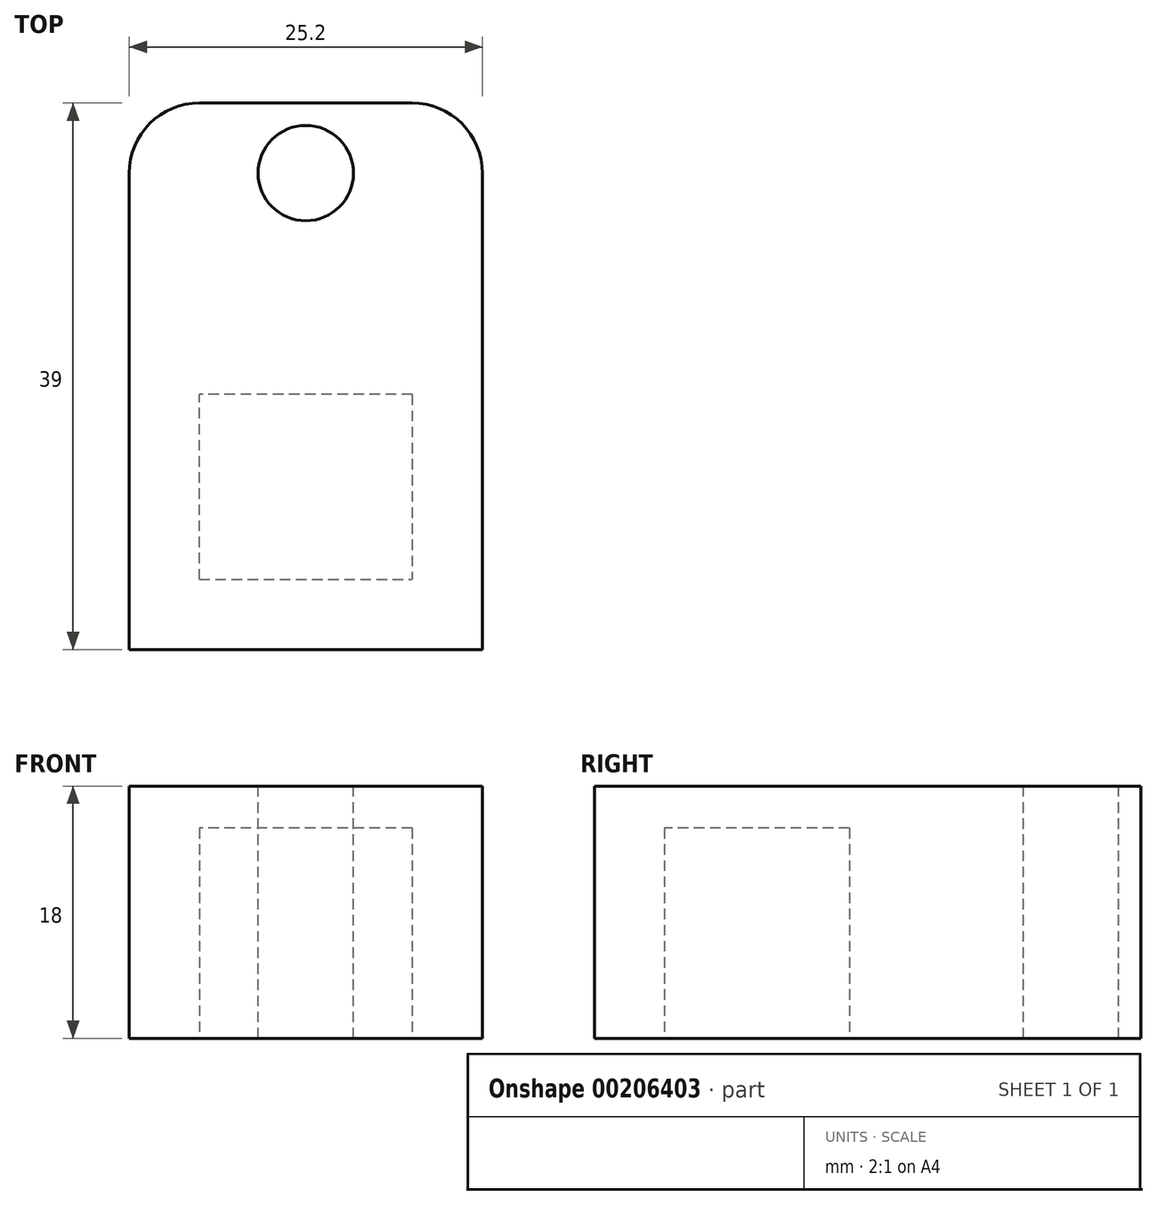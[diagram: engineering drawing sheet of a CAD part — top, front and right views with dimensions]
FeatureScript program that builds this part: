
annotation { "Feature Type Name" : "Feature", "Feature Type Description" : "" }
export const myFeature = defineFeature(function(context is Context, id is Id, definition is map)
    precondition{}
    {
        {
            var Q0;
            Q0=qCreatedBy(makeId("Top.planeOp"),FACE);
            var sketch = newSketch(context, id + "F0", { "sketchPlane" : qUnion([Q0])});
            skLineSegment(sketch, "E0", {"start": v(0, 6.6) * mm, "end": v(-7.6, 6.6) * mm});
            skLineSegment(sketch, "E1", {"start": v(-7.6, 6.6) * mm, "end": v(-7.6, 0) * mm});
            skLineSegment(sketch, "E2.MirrorCS", {"start": v(7.6, 6.6) * mm, "end": v(7.6, 0) * mm});
            skLineSegment(sketch, "E3.MirrorCS", {"start": v(0, 6.6) * mm, "end": v(7.6, 6.6) * mm});
            skLineSegment(sketch, "E4.MirrorCS", {"start": v(7.6, -6.6) * mm, "end": v(7.6, 0) * mm});
            skLineSegment(sketch, "E5.MirrorCS", {"start": v(0, -6.6) * mm, "end": v(7.6, -6.6) * mm});
            skLineSegment(sketch, "E6.MirrorCS", {"start": v(0, -6.6) * mm, "end": v(-7.6, -6.6) * mm});
            skLineSegment(sketch, "E7.MirrorCS", {"start": v(-7.6, -6.6) * mm, "end": v(-7.6, 0) * mm});
            skLineSegment(sketch, "E8", {"start": v(12.6, 22.4) * mm, "end": v(12.6, 0) * mm});
            skLineSegment(sketch, "E9", {"start": v(12.6, 0) * mm, "end": v(12.6, -11.6) * mm});
            skLineSegment(sketch, "E10", {"start": v(12.6, -11.6) * mm, "end": v(0, -11.6) * mm});
            skLineSegment(sketch, "E11", {"start": v(7.6, 27.4) * mm, "end": v(0, 27.4) * mm});
            skPoint(sketch, "E12.visualSharp", {"position": v(12.6, 27.4) * mm});
            skArc(sketch, "E12.filletArc", {"start": v(12.6, 22.4) * mm, "mid": v(11.14, 25.94) * mm, "end": v(7.6, 27.4) * mm});
            skLineSegment(sketch, "E13.MirrorCS", {"start": v(-7.6, 27.4) * mm, "end": v(0, 27.4) * mm});
            skArc(sketch, "E14.MirrorCS", {"start": v(-12.6, 22.4) * mm, "mid": v(-11.14, 25.94) * mm, "end": v(-7.6, 27.4) * mm});
            skLineSegment(sketch, "E15.MirrorCS", {"start": v(-12.6, 22.4) * mm, "end": v(-12.6, 0) * mm});
            skLineSegment(sketch, "E16.MirrorCS", {"start": v(-12.6, 0) * mm, "end": v(-12.6, -11.6) * mm});
            skLineSegment(sketch, "E17.MirrorCS", {"start": v(-12.6, -11.6) * mm, "end": v(0, -11.6) * mm});
            skSolve(sketch);
        }
        {
            var Q0;
            Q0 = qSketchRegion(id + "F0", true);
            extrude(context, id + "F1", {"entities" : qUnion([Q0]), "depth" : 15 * mm});
        }
        {
            var Q0;
            Q0=makeQuery(id+"F1.opExtrude","CAP_FACE",FACE,{"disambiguationData":[OSD([sQuery(id+"F0.wireOp",EDGE,"E0"),sQuery(id+"F0.wireOp",EDGE,"E1"),sQuery(id+"F0.wireOp",EDGE,"E2.MirrorCS"),sQuery(id+"F0.wireOp",EDGE,"E3.MirrorCS"),sQuery(id+"F0.wireOp",EDGE,"E4.MirrorCS"),sQuery(id+"F0.wireOp",EDGE,"E5.MirrorCS"),sQuery(id+"F0.wireOp",EDGE,"E6.MirrorCS"),sQuery(id+"F0.wireOp",EDGE,"E7.MirrorCS"),sQuery(id+"F0.wireOp",EDGE,"E8"),sQuery(id+"F0.wireOp",EDGE,"E9"),sQuery(id+"F0.wireOp",EDGE,"E10"),sQuery(id+"F0.wireOp",EDGE,"E11"),sQuery(id+"F0.wireOp",EDGE,"E12.filletArc"),sQuery(id+"F0.wireOp",EDGE,"E13.MirrorCS"),sQuery(id+"F0.wireOp",EDGE,"E14.MirrorCS"),sQuery(id+"F0.wireOp",EDGE,"E15.MirrorCS"),sQuery(id+"F0.wireOp",EDGE,"E16.MirrorCS"),sQuery(id+"F0.wireOp",EDGE,"E17.MirrorCS")])],"isStart":false});
            var sketch = newSketch(context, id + "F2", { "sketchPlane" : qUnion([Q0])});
            skLineSegment(sketch, "E18", {"start": v(-12.6, -11.6) * mm, "end": v(-12.6, 22.4) * mm});
            skLineSegment(sketch, "E19", {"start": v(-7.6, 27.4) * mm, "end": v(0, 27.4) * mm});
            skLineSegment(sketch, "E20", {"start": v(-12.6, -11.6) * mm, "end": v(0, -11.6) * mm});
            skPoint(sketch, "E21.visualSharp", {"position": v(-12.6, 27.4) * mm});
            skArc(sketch, "E21.filletArc", {"start": v(-7.6, 27.4) * mm, "mid": v(-11.14, 25.94) * mm, "end": v(-12.6, 22.4) * mm});
            skLineSegment(sketch, "E22.MirrorCS", {"start": v(7.6, 27.4) * mm, "end": v(0, 27.4) * mm});
            skArc(sketch, "E23.MirrorCS", {"start": v(7.6, 27.4) * mm, "mid": v(11.14, 25.94) * mm, "end": v(12.6, 22.4) * mm});
            skLineSegment(sketch, "E24.MirrorCS", {"start": v(12.6, -11.6) * mm, "end": v(12.6, 22.4) * mm});
            skLineSegment(sketch, "E25.MirrorCS", {"start": v(12.6, -11.6) * mm, "end": v(0, -11.6) * mm});
            skSolve(sketch);
        }
        {
            var Q0;
            Q0 = qSketchRegion(id + "F2", true);
            extrude(context, id + "F3", {"entities" : qUnion([Q0]), "operationType" : NewBodyOperationType.ADD, "depth" : 3 * mm});
        }
        {
            var Q0;
            Q0=makeQuery(id+"F3.opExtrude","CAP_FACE",FACE,{"disambiguationData":[OSD([sQuery(id+"F2.wireOp",EDGE,"E18"),sQuery(id+"F2.wireOp",EDGE,"E19"),sQuery(id+"F2.wireOp",EDGE,"E20"),sQuery(id+"F2.wireOp",EDGE,"E21.filletArc"),sQuery(id+"F2.wireOp",EDGE,"E22.MirrorCS"),sQuery(id+"F2.wireOp",EDGE,"E23.MirrorCS"),sQuery(id+"F2.wireOp",EDGE,"E24.MirrorCS"),sQuery(id+"F2.wireOp",EDGE,"E25.MirrorCS")])],"isStart":false});
            var sketch = newSketch(context, id + "F4", { "sketchPlane" : qUnion([Q0])});
            skCircle(sketch, "E26", {"center": v(0, 22.4) * mm, "radius": 3.4 * mm});
            skSolve(sketch);
        }
        {
            var Q0;
            Q0 = qSketchRegion(id + "F4", true);
            extrude(context, id + "F5", {"entities" : qUnion([Q0]), "operationType" : NewBodyOperationType.REMOVE, "endBound" : BoundingType.THROUGH_ALL, "oppositeDirection" : true, "depth" : 25 * mm});
        }
    });
